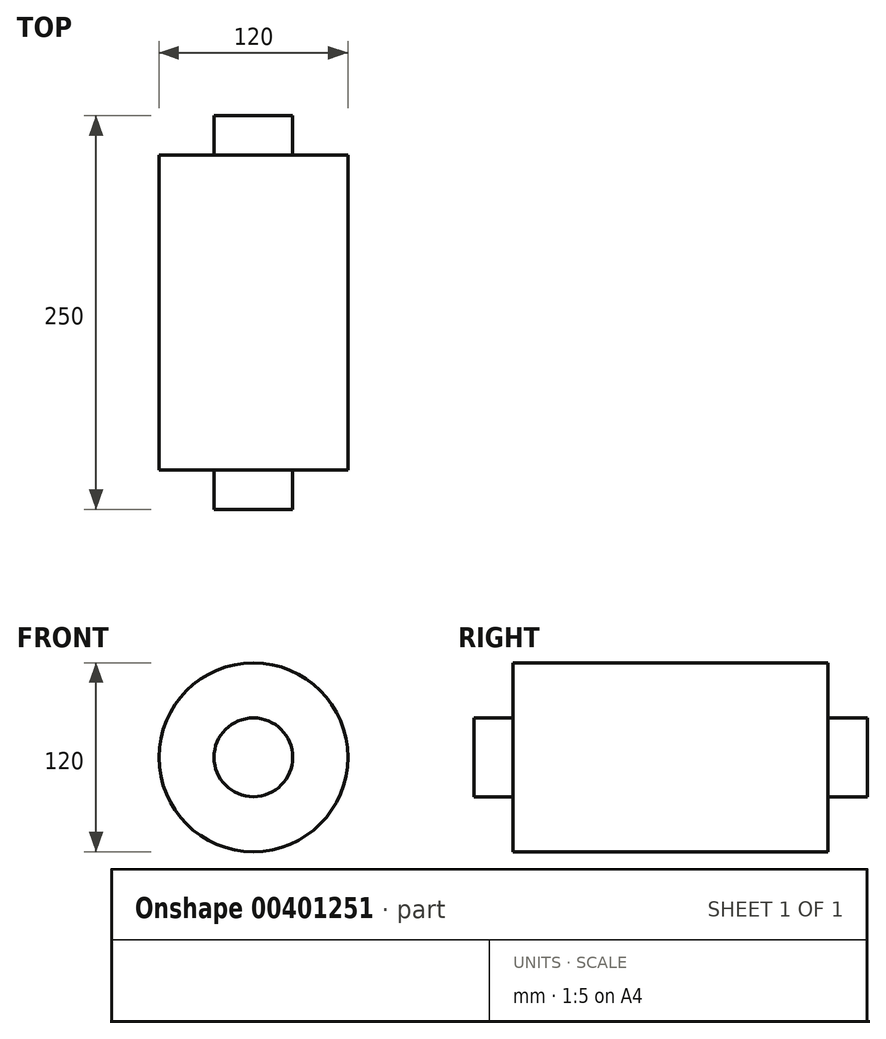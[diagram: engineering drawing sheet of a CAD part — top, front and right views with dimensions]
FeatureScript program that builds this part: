
annotation { "Feature Type Name" : "Feature", "Feature Type Description" : "" }
export const myFeature = defineFeature(function(context is Context, id is Id, definition is map)
    precondition{}
    {
        {
            var Q0;
            Q0=qCreatedBy(makeId("Right.planeOp"),FACE);
            var sketch = newSketch(context, id + "F0", { "sketchPlane" : qUnion([Q0])});
            skLineSegment(sketch, "E0", {"start": v(-125, 0) * mm, "end": v(125, 0) * mm});
            skLineSegment(sketch, "E1", {"start": v(-125, 0) * mm, "end": v(-125, 25) * mm});
            skLineSegment(sketch, "E2", {"start": v(-125, 25) * mm, "end": v(-100, 25) * mm});
            skLineSegment(sketch, "E3", {"start": v(-100, 25) * mm, "end": v(-100, 60) * mm});
            skLineSegment(sketch, "E4", {"start": v(-100, 60) * mm, "end": v(100, 60) * mm});
            skLineSegment(sketch, "E5", {"start": v(0, 0) * mm, "end": v(0, 60) * mm, "construction": true});
            skLineSegment(sketch, "E6.MirrorCS", {"start": v(125, 0) * mm, "end": v(125, 25) * mm});
            skLineSegment(sketch, "E7.MirrorCS", {"start": v(100, 25) * mm, "end": v(100, 60) * mm});
            skLineSegment(sketch, "E8.MirrorCS", {"start": v(125, 25) * mm, "end": v(100, 25) * mm});
            skSolve(sketch);
        }
        {
            var Q0;
            Q0 = qSketchRegion(id + "F0", true);
            var Q1;
            Q1=sQuery(id+"F0.wireOp",EDGE,"E0");
            revolve(context, id + "F1", {"entities" : qUnion([Q0]), "axis" : qUnion([Q1]), "revolveType" : RevolveType.FULL, "oppositeDirection" : true});
        }
    });
